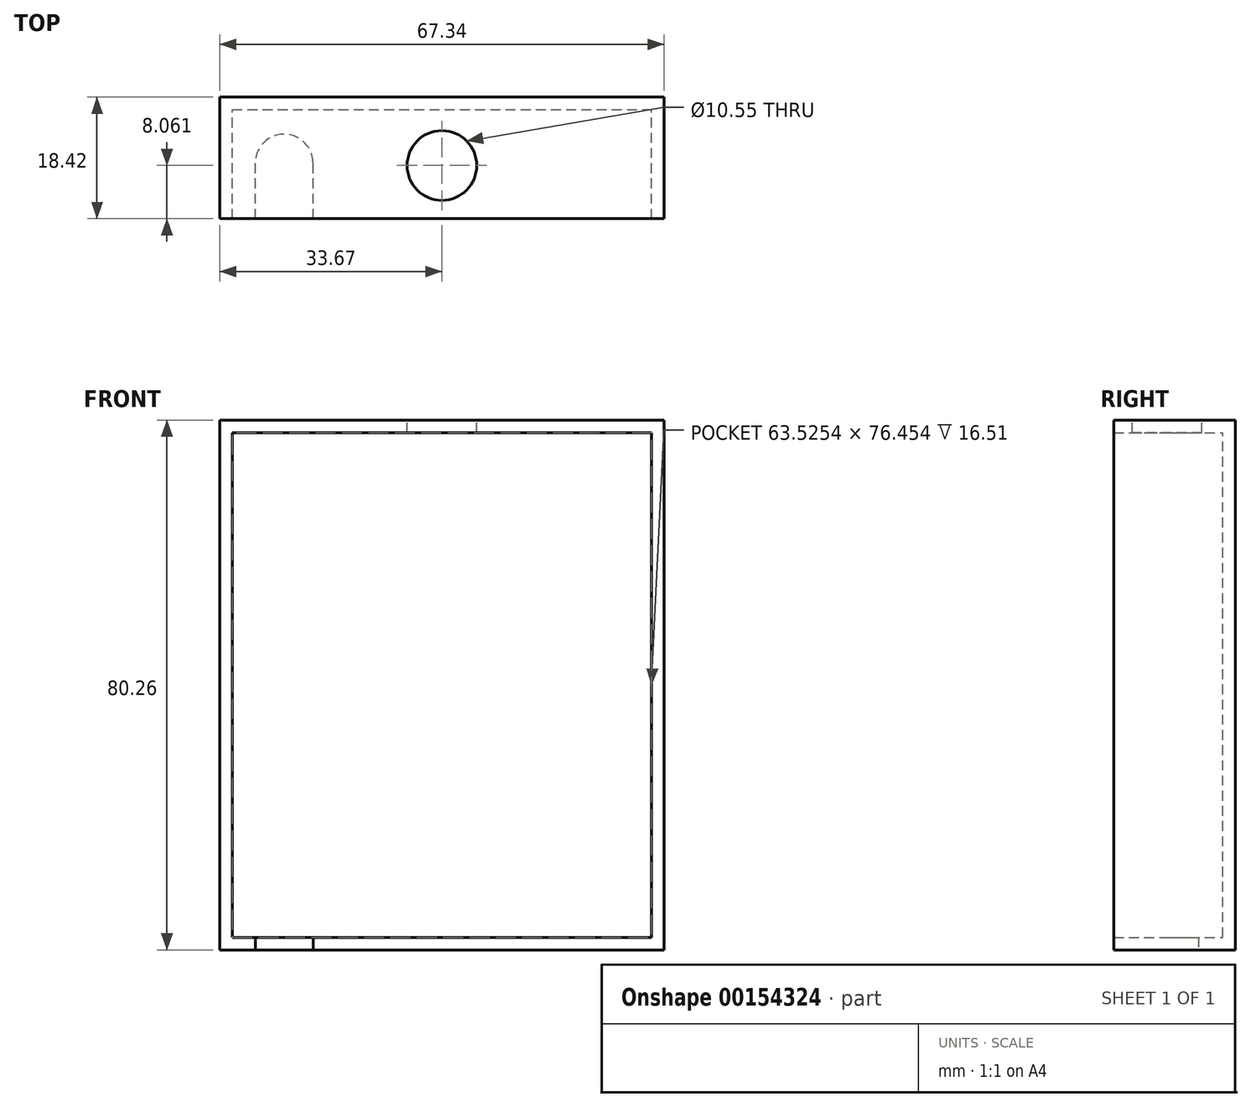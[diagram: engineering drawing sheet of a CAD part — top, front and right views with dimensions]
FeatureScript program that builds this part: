
annotation { "Feature Type Name" : "Feature", "Feature Type Description" : "" }
export const myFeature = defineFeature(function(context is Context, id is Id, definition is map)
    precondition{}
    {
        {
            var Q0;
            Q0=qCreatedBy(makeId("Front.planeOp"),FACE);
            var sketch = newSketch(context, id + "F0", { "sketchPlane" : qUnion([Q0])});
            skLineSegment(sketch, "E0.bottom", {"start": v(0, -29.98) * mm, "end": v(31.76, -29.98) * mm});
            skLineSegment(sketch, "E0.top", {"start": v(0, 46.47) * mm, "end": v(31.76, 46.47) * mm});
            skLineSegment(sketch, "E0.left", {"start": v(0, -29.98) * mm, "end": v(0, 46.47) * mm});
            skLineSegment(sketch, "E0.right", {"start": v(31.76, -29.98) * mm, "end": v(31.76, 46.47) * mm});
            skLineSegment(sketch, "E1.bottom", {"start": v(0, 46.47) * mm, "end": v(-31.76, 46.47) * mm});
            skLineSegment(sketch, "E1.top", {"start": v(0, -29.98) * mm, "end": v(-31.76, -29.98) * mm});
            skLineSegment(sketch, "E1.left", {"start": v(0, 46.47) * mm, "end": v(0, -29.98) * mm});
            skLineSegment(sketch, "E1.right", {"start": v(-31.76, 46.47) * mm, "end": v(-31.76, -29.98) * mm});
            skSolve(sketch);
        }
        {
            var Q0;
            Q0 = qSketchRegion(id + "F0", true);
            extrude(context, id + "F1", {"entities" : qUnion([Q0]), "depth" : 16.5 * mm});
        }
        {
            var Q0;
            Q0=makeQuery(id+"F1.opExtrude","CAP_FACE",FACE,{"disambiguationData":[OSD([sQuery(id+"F0.wireOp",EDGE,"E0.bottom"),sQuery(id+"F0.wireOp",EDGE,"E0.top"),sQuery(id+"F0.wireOp",EDGE,"E0.right"),sQuery(id+"F0.wireOp",EDGE,"E1.bottom"),sQuery(id+"F0.wireOp",EDGE,"E1.top"),sQuery(id+"F0.wireOp",EDGE,"E1.right")])],"isStart":false});
            shell(context, id + "F2", {"entities" : qUnion([Q0]), "thickness" : 1.9 * mm, "oppositeDirection" : true});
        }
        {
            var Q0;
            Q0=makeQuery(id+"F1.opExtrude","SWEPT_FACE",FACE,{"disambiguationData":[OSD([sQuery(id+"F0.wireOp",EDGE,"E0.top"),sQuery(id+"F0.wireOp",EDGE,"E1.bottom")])]});
            var sketch = newSketch(context, id + "F3", { "sketchPlane" : qUnion([Q0])});
            skCircle(sketch, "E2", {"center": v(0, -8.45) * mm, "radius": 5.28 * mm});
            skSolve(sketch);
        }
        {
            var Q0;
            Q0 = qSketchRegion(id + "F3", true);
            extrude(context, id + "F4", {"entities" : qUnion([Q0]), "operationType" : NewBodyOperationType.REMOVE, "oppositeDirection" : true, "depth" : 25.4 * mm});
        }
        {
            var Q0;
            Q0=makeQuery(id+"F1.opExtrude","SWEPT_FACE",FACE,{"disambiguationData":[OSD([sQuery(id+"F0.wireOp",EDGE,"E0.bottom"),sQuery(id+"F0.wireOp",EDGE,"E1.top")])]});
            var sketch = newSketch(context, id + "F5", { "sketchPlane" : qUnion([Q0])});
            skCircle(sketch, "E3", {"center": v(-23.9, 8.08) * mm, "radius": 4.38 * mm});
            skSolve(sketch);
        }
        {
            var Q0;
            Q0 = qSketchRegion(id + "F5", true);
            extrude(context, id + "F6", {"entities" : qUnion([Q0]), "operationType" : NewBodyOperationType.REMOVE, "oppositeDirection" : true, "depth" : 25.4 * mm});
        }
        {
            var Q0;
            Q0=makeQuery(id+"F1.opExtrude","SWEPT_BODY",BODY,{"disambiguationData":[OSD([sQuery(id+"F0.wireOp",EDGE,"E0.bottom"),sQuery(id+"F0.wireOp",EDGE,"E0.top"),sQuery(id+"F0.wireOp",EDGE,"E0.right"),sQuery(id+"F0.wireOp",EDGE,"E1.bottom"),sQuery(id+"F0.wireOp",EDGE,"E1.top"),sQuery(id+"F0.wireOp",EDGE,"E1.right")])]});
            transform(context, id + "F7", {"entities" : qUnion([Q0]), "transformType" : TransformType.TRANSLATION_3D, "dx" : 0 * mm, "dy" : 0 * mm, "dz" : 31.1 * mm, "makeCopy" : false});
        }
        {
            var Q0;
            Q0=makeQuery(id+"F1.opExtrude","SWEPT_FACE",FACE,{"disambiguationData":[OSD([sQuery(id+"F0.wireOp",EDGE,"E0.bottom"),sQuery(id+"F0.wireOp",EDGE,"E1.top")])]});
            var sketch = newSketch(context, id + "F8", { "sketchPlane" : qUnion([Q0])});
            skLineSegment(sketch, "E4", {"start": v(-19.52, 8.08) * mm, "end": v(-19.52, 16.51) * mm});
            skLineSegment(sketch, "E5", {"start": v(-28.28, 8.08) * mm, "end": v(-28.28, 16.51) * mm});
            skLineSegment(sketch, "E6", {"start": v(-28.28, 16.51) * mm, "end": v(-19.52, 16.51) * mm});
            skLineSegment(sketch, "E7", {"start": v(-19.52, 8.08) * mm, "end": v(-28.28, 8.08) * mm});
            skSolve(sketch);
        }
        {
            var Q0;
            Q0 = qSketchRegion(id + "F8", true);
            extrude(context, id + "F9", {"entities" : qUnion([Q0]), "operationType" : NewBodyOperationType.REMOVE, "oppositeDirection" : true, "depth" : 25.4 * mm});
        }
    });
